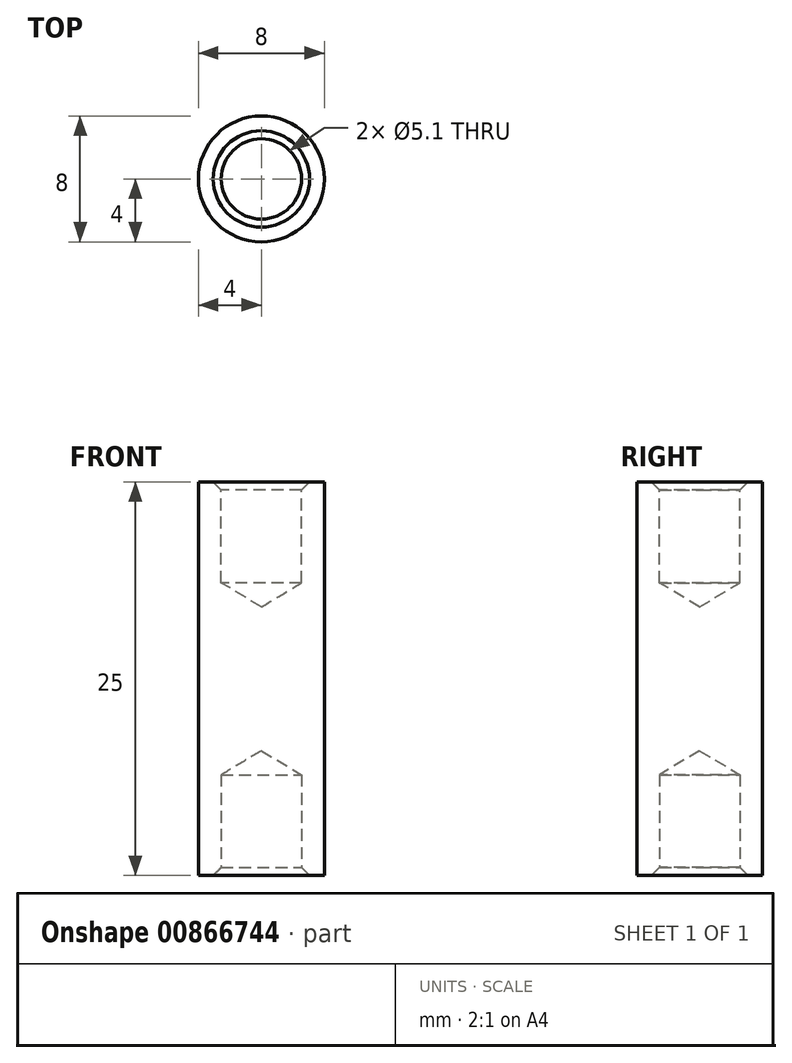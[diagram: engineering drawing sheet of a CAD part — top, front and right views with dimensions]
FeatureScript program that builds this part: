
annotation { "Feature Type Name" : "Feature", "Feature Type Description" : "" }
export const myFeature = defineFeature(function(context is Context, id is Id, definition is map)
    precondition{}
    {
        {
            assignVariable(context, id + "F0", {"variableType" : VariableType.LENGTH, "name" : "PillarHeight", "lengthValue" : 25 * mm});
        }
        {
            assignVariable(context, id + "F1", {"variableType" : VariableType.LENGTH, "name" : "InsertWidth", "lengthValue" : 5.1 * mm});
        }
        {
            assignVariable(context, id + "F2", {"variableType" : VariableType.LENGTH, "name" : "InsertDepth", "lengthValue" : 6.4 * mm});
        }
        {
            var Q0;
            Q0=qCreatedBy(makeId("Top.planeOp"),FACE);
            var sketch = newSketch(context, id + "F3", { "sketchPlane" : qUnion([Q0])});
            skCircle(sketch, "E0", {"center": v(0, 0) * mm, "radius": 4 * mm});
            skSolve(sketch);
        }
        {
            var Q0;
            Q0=makeQuery(id+"F3.imprint","IMPRINT",FACE,{"disambiguationData":[TD([[makeQuery(id+"F3.imprint","IMPRINT",EDGE,{"derivedFrom":sQuery(id+"F3.wireOp",EDGE,"E0")}),1.0]])]});
            extrude(context, id + "F4", {"entities" : qUnion([Q0]), "depth" : getVariable(context, 'PillarHeight'), "offsetDistance" : 25 * mm});
        }
        {
            var Q0;
            Q0=makeQuery(id+"F4.opExtrude","CAP_FACE",FACE,{"disambiguationData":[OSD([sQuery(id+"F3.wireOp",EDGE,"E0")])],"isStart":false});
            var sketch = newSketch(context, id + "F5", { "sketchPlane" : qUnion([Q0])});
            skPoint(sketch, "E1", {"position": v(0, 0) * mm});
            skSolve(sketch);
        }
        {
            var Q0;
            Q0=sQuery(id+"F5.wireOp",VERTEX,"E1");
            var Q1;
            Q1=makeQuery(id+"F4.opExtrude","SWEPT_BODY",BODY,{"disambiguationData":[OSD([sQuery(id+"F3.wireOp",EDGE,"E0")])]});
            hole(context, id + "F6", {"style" : HoleStyle.C_SINK, "endStyle" : HoleEndStyle.BLIND, "holeDiameter" : getVariable(context, 'InsertWidth'), "cSinkDiameter" : (getVariable(context, 'InsertWidth') * 1.2), "cSinkAngle" : 90 * degree, "majorDiameter" : 5 * mm, "holeDepth" : getVariable(context, 'InsertDepth'), "isTappedThrough" : true, "tappedDepth" : 12 * mm, "tapClearance" : 3, "startFromSketch" : true, "locations" : qUnion([Q0]), "scope" : qUnion([Q1])});
        }
        {
            var Q0;
            Q0=sQuery(id+"F3.wireOp",VERTEX,"E0.center");
            var Q1;
            Q1=makeQuery(id+"F4.opExtrude","SWEPT_BODY",BODY,{"disambiguationData":[OSD([sQuery(id+"F3.wireOp",EDGE,"E0")])]});
            hole(context, id + "F7", {"style" : HoleStyle.C_SINK, "endStyle" : HoleEndStyle.BLIND, "oppositeDirection" : true, "holeDiameter" : getVariable(context, 'InsertWidth'), "cSinkDiameter" : (getVariable(context, 'InsertWidth') * 1.2), "cSinkAngle" : 90 * degree, "majorDiameter" : 5 * mm, "holeDepth" : getVariable(context, 'InsertDepth'), "isTappedThrough" : true, "tappedDepth" : 12 * mm, "tapClearance" : 3, "startFromSketch" : true, "locations" : qUnion([Q0]), "scope" : qUnion([Q1])});
        }
    });
